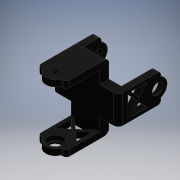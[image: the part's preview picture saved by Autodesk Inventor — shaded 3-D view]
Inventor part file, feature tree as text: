
AUTODESK INVENTOR PART (.ipt)
format: ipt  version: 2016 (Build 200138000, 138)  size: 395,264 bytes
history: native  units: mm
features: extrude x14, sketch x14, fillet x2, other x1
ambient origin geometry x8: Origin, YZ Plane, XZ Plane, XY Plane, X Axis, Y Axis, Z Axis, Center Point
bodies: Body1 (feature_tree)
feature tree (31):
  other  "ソリッド1"
  extrude  "押し出し1"  Depth=18.0mm
  extrude  "押し出し2"  Depth=41.8mm
  extrude  "押し出し3"  Depth=41.8mm
  extrude  "押し出し4"  Depth=18.0mm
  extrude  "押し出し5"  Depth=6.0mm TaperAngle=0.0deg
  extrude  "押し出し6"  Depth=4.0mm
  extrude  "押し出し7"  Depth=4.0mm
  extrude  "押し出し8"  Depth=25.0mm TaperAngle=0.0deg
  extrude  "押し出し9"  Depth=4.0mm
  extrude  "押し出し10"  Depth=4.0mm
  extrude  "押し出し11"  Depth=25.0mm TaperAngle=0.0deg
  extrude  "押し出し12"  Depth=25.0mm
  extrude  "押し出し13"  Depth=12.0mm
  extrude  "押し出し14"  Depth=2.0mm
  fillet  "フィレット1"  Radius=2.0mm
  fillet  "フィレット2"  Radius=6.0mm
  sketch  "スケッチ1"
  sketch  "スケッチ2"
  sketch  "スケッチ3"
  sketch  "スケッチ4"
  sketch  "スケッチ5"
  sketch  "スケッチ6"
  sketch  "スケッチ7"
  sketch  "スケッチ8"
  sketch  "スケッチ9"
  sketch  "スケッチ10"
  sketch  "スケッチ11"
  sketch  "スケッチ12"
  sketch  "スケッチ13"
  sketch  "スケッチ14"
